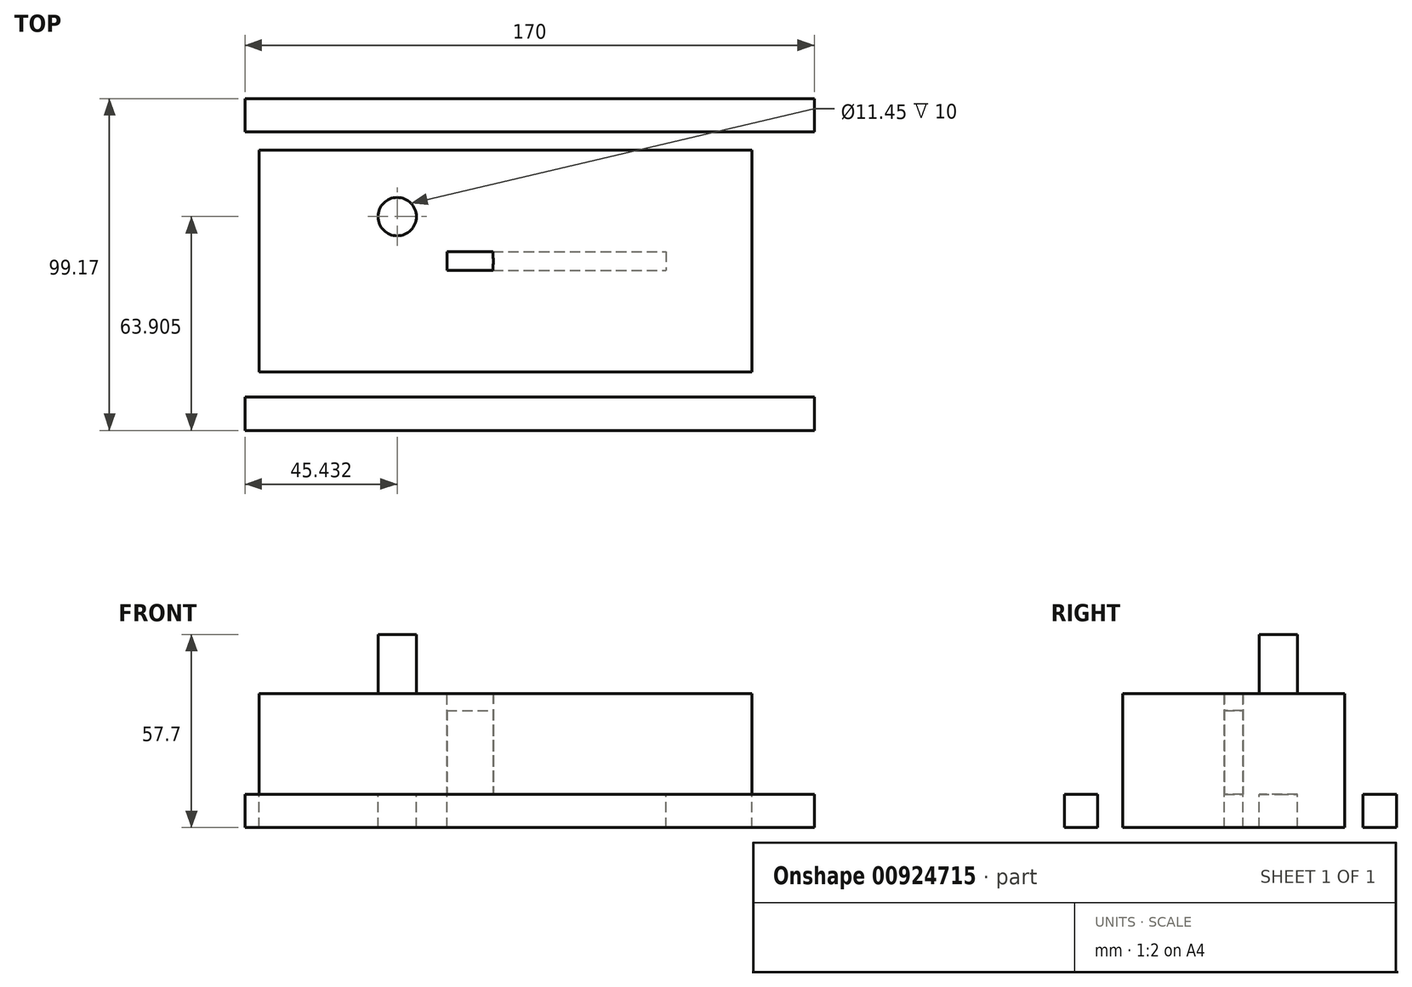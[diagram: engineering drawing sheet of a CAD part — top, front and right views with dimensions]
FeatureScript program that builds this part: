
annotation { "Feature Type Name" : "Feature", "Feature Type Description" : "" }
export const myFeature = defineFeature(function(context is Context, id is Id, definition is map)
    precondition{}
    {
        {
            var Q0;
            Q0=qCreatedBy(makeId("Top.planeOp"),FACE);
            var sketch = newSketch(context, id + "F0", { "sketchPlane" : qUnion([Q0])});
            skLineSegment(sketch, "E0.bottom", {"start": v(-102.5, 55) * mm, "end": v(102.5, 55) * mm});
            skLineSegment(sketch, "E0.top", {"start": v(-102.5, -55) * mm, "end": v(102.5, -55) * mm});
            skLineSegment(sketch, "E0.left", {"start": v(-102.5, 55) * mm, "end": v(-102.5, -55) * mm});
            skLineSegment(sketch, "E0.right", {"start": v(102.5, 55) * mm, "end": v(102.5, -55) * mm});
            skPoint(sketch, "E0.middle", {"position": v(0, 0) * mm});
            skCircle(sketch, "E1", {"center": v(-41.23, 0) * mm, "radius": 28.67 * mm});
            skLineSegment(sketch, "E2.bottom", {"start": v(64.73, 33.15) * mm, "end": v(-82.5, 33.15) * mm});
            skLineSegment(sketch, "E2.top", {"start": v(64.73, -33.15) * mm, "end": v(-82.5, -33.15) * mm});
            skLineSegment(sketch, "E2.left", {"start": v(64.73, 33.15) * mm, "end": v(64.73, -33.15) * mm});
            skLineSegment(sketch, "E2.right", {"start": v(-82.5, 33.15) * mm, "end": v(-82.5, -33.15) * mm});
            skPoint(sketch, "E2.middle", {"position": v(-8.89, 0) * mm});
            skLineSegment(sketch, "E3.bottom", {"start": v(-86.66, 48.6) * mm, "end": v(83.34, 48.6) * mm});
            skLineSegment(sketch, "E3.top", {"start": v(-86.66, 38.6) * mm, "end": v(83.34, 38.6) * mm});
            skLineSegment(sketch, "E3.left", {"start": v(-86.66, 48.6) * mm, "end": v(-86.66, 38.6) * mm});
            skLineSegment(sketch, "E3.right", {"start": v(83.34, 48.6) * mm, "end": v(83.34, 38.6) * mm});
            skLineSegment(sketch, "E4.bottom", {"start": v(-86.66, -40.58) * mm, "end": v(83.34, -40.58) * mm});
            skLineSegment(sketch, "E4.top", {"start": v(-86.66, -50.58) * mm, "end": v(83.34, -50.58) * mm});
            skLineSegment(sketch, "E4.left", {"start": v(-86.66, -40.58) * mm, "end": v(-86.66, -50.58) * mm});
            skLineSegment(sketch, "E4.right", {"start": v(83.34, -40.58) * mm, "end": v(83.34, -50.58) * mm});
            skCircle(sketch, "E5", {"center": v(-41.23, 13.33) * mm, "radius": 5.73 * mm});
            skLineSegment(sketch, "E6.bottom", {"start": v(-26.37, 2.78) * mm, "end": v(39.11, 2.78) * mm});
            skLineSegment(sketch, "E6.top", {"start": v(-26.37, -2.78) * mm, "end": v(39.11, -2.78) * mm});
            skLineSegment(sketch, "E6.left", {"start": v(-26.37, 2.78) * mm, "end": v(-26.37, -2.78) * mm});
            skLineSegment(sketch, "E6.right", {"start": v(39.11, 2.78) * mm, "end": v(39.11, -2.78) * mm});
            skPoint(sketch, "E6.middle", {"position": v(6.37, 0) * mm});
            skSolve(sketch);
        }
        {
            var Q0;
            Q0=makeQuery(id+"F0.imprint","IMPRINT",FACE,{"disambiguationData":[TD([[makeQuery(id+"F0.imprint","IMPRINT",EDGE,{"derivedFrom":sQuery(id+"F0.wireOp",EDGE,"E5")}),-1.0]])]});
            var Q1;
            Q1=makeQuery(id+"F0.imprint","IMPRINT",FACE,{"disambiguationData":[TD([[makeQuery(id+"F0.imprint","IMPRINT",EDGE,{"derivedFrom":sQuery(id+"F0.wireOp",EDGE,"E4.bottom")}),-1.0]])]});
            var Q2;
            Q2=makeQuery(id+"F0.imprint","IMPRINT",FACE,{"disambiguationData":[TD([[makeQuery(id+"F0.imprint","IMPRINT",EDGE,{"derivedFrom":sQuery(id+"F0.wireOp",EDGE,"E3.bottom")}),-1.0]])]});
            var Q3;
            Q3=makeQuery(id+"F0.imprint","IMPRINT",FACE,{"disambiguationData":[TD([[makeQuery(id+"F0.imprint","IMPRINT",EDGE,{"derivedFrom":sQuery(id+"F0.wireOp",EDGE,"E2.bottom")}),1.0]])]});
            extrude(context, id + "F1", {"entities" : qUnion([Q0, Q1, Q2, Q3]), "oppositeDirection" : true, "depth" : 10 * mm, "offsetDistance" : 25 * mm});
        }
        {
            var Q0;
            Q0=makeQuery(id+"F0.imprint","IMPRINT",FACE,{"disambiguationData":[TD([[makeQuery(id+"F0.imprint","IMPRINT",EDGE,{"derivedFrom":sQuery(id+"F0.wireOp",EDGE,"E5")}),-1.0]])]});
            var Q1;
            Q1=makeQuery(id+"F1.opExtrude","CAP_FACE",FACE,{"disambiguationData":[OSD([sQuery(id+"F0.wireOp",EDGE,"E1"),sQuery(id+"F0.wireOp",EDGE,"E5"),sQuery(id+"F0.wireOp",EDGE,"E6.bottom"),sQuery(id+"F0.wireOp",EDGE,"E6.top"),sQuery(id+"F0.wireOp",EDGE,"E6.left")])],"isStart":true});
            var Q2;
            Q2=makeQuery(id+"F1.opExtrude","CAP_FACE",FACE,{"disambiguationData":[OSD([sQuery(id+"F0.wireOp",EDGE,"E1"),sQuery(id+"F0.wireOp",EDGE,"E5"),sQuery(id+"F0.wireOp",EDGE,"E6.bottom"),sQuery(id+"F0.wireOp",EDGE,"E6.top"),sQuery(id+"F0.wireOp",EDGE,"E6.left")])],"isStart":false});
            var Q3;
            {var subQ5=sQuery(id+"F0.wireOp",EDGE,"E6.right");Q3=makeQuery(id+"F0.imprint","IMPRINT",FACE,{"disambiguationData":[TD([[makeQuery(id+"F0.imprint","IMPRINT",EDGE,{"derivedFrom":subQ5}),-1.0]])]});}
            extrude(context, id + "F2", {"entities" : qUnion([Q0, Q1, Q2, Q3]), "operationType" : NewBodyOperationType.ADD, "depth" : 30 * mm, "offsetDistance" : 25 * mm});
        }
        {
            var Q0;
            {var subQ5=sQuery(id+"F0.wireOp",EDGE,"E6.left");Q0=makeQuery(id+"F0.imprint","IMPRINT",FACE,{"disambiguationData":[TD([[makeQuery(id+"F0.imprint","IMPRINT",EDGE,{"derivedFrom":subQ5}),1.0]])]});}
            extrude(context, id + "F3", {"entities" : qUnion([Q0]), "depth" : 25 * mm, "offsetDistance" : 25 * mm});
        }
        {
            var Q0;
            Q0=makeQuery(id+"F0.imprint","IMPRINT",FACE,{"disambiguationData":[TD([[makeQuery(id+"F0.imprint","IMPRINT",EDGE,{"derivedFrom":sQuery(id+"F0.wireOp",EDGE,"E5")}),1.0]])]});
            extrude(context, id + "F4", {"entities" : qUnion([Q0]), "operationType" : NewBodyOperationType.ADD, "depth" : 47.7 * mm, "offsetDistance" : 25 * mm});
        }
        {
            var Q0;
            Q0=sQuery(id+"F0.wireOp",EDGE,"E1");
            extrude(context, id + "F5", {"bodyType" : ToolBodyType.SURFACE, "surfaceEntities" : qUnion([Q0]), "depth" : 27 * mm, "offsetDistance" : 25 * mm});
        }
        {
            var Q0;
            Q0=sQuery(id+"F0.wireOp",EDGE,"E1");
            extrude(context, id + "F6", {"bodyType" : ToolBodyType.SURFACE, "surfaceOperationType" : NewSurfaceOperationType.ADD, "surfaceEntities" : qUnion([Q0]), "depth" : 27 * mm, "offsetDistance" : 25 * mm});
        }
    });
